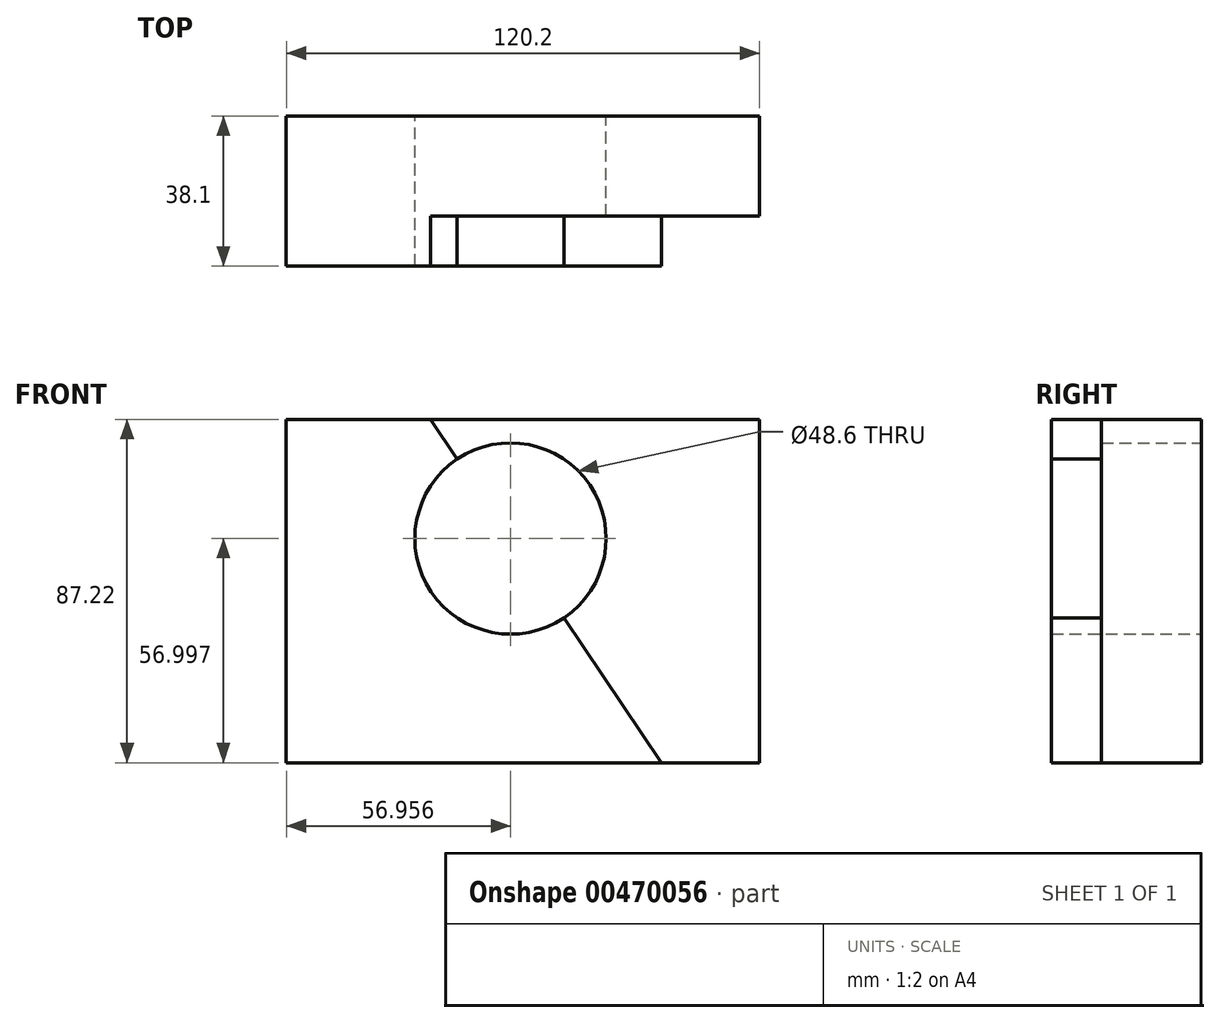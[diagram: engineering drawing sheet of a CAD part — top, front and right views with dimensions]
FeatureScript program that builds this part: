
annotation { "Feature Type Name" : "Feature", "Feature Type Description" : "" }
export const myFeature = defineFeature(function(context is Context, id is Id, definition is map)
    precondition{}
    {
        {
            var Q0;
            Q0=qCreatedBy(makeId("Front.planeOp"),FACE);
            var sketch = newSketch(context, id + "F0", { "sketchPlane" : qUnion([Q0])});
            skLineSegment(sketch, "E0.bottom", {"start": v(60.1, 43.6) * mm, "end": v(-60.1, 43.6) * mm});
            skLineSegment(sketch, "E0.top", {"start": v(60.1, -43.6) * mm, "end": v(-60.1, -43.6) * mm});
            skLineSegment(sketch, "E0.left", {"start": v(60.1, 43.6) * mm, "end": v(60.1, -43.6) * mm});
            skLineSegment(sketch, "E0.right", {"start": v(-60.1, 43.6) * mm, "end": v(-60.1, -43.6) * mm});
            skPoint(sketch, "E0.middle", {"position": v(0, 0) * mm});
            skLineSegment(sketch, "E1", {"start": v(-23.51, 43.6) * mm, "end": v(-16.72, 33.54) * mm});
            skCircle(sketch, "E2", {"center": v(-3.14, 13.39) * mm, "radius": 24.3 * mm});
            skLineSegment(sketch, "E3.trimOffspring", {"start": v(10.44, -6.76) * mm, "end": v(35.27, -43.6) * mm});
            skSolve(sketch);
        }
        {
            var Q0;
            {var subQ0=sQuery(id+"F0.wireOp",EDGE,"E0.right");Q0=makeQuery(id+"F0.imprint","IMPRINT",FACE,{"disambiguationData":[TD([[makeQuery(id+"F0.imprint","IMPRINT",EDGE,{"derivedFrom":subQ0}),1.0]])]});}
            extrude(context, id + "F1", {"entities" : qUnion([Q0]), "depth" : 38.1 * mm});
        }
        {
            var Q0;
            {var subQ1=sQuery(id+"F0.wireOp",EDGE,"E0.left");Q0=makeQuery(id+"F0.imprint","IMPRINT",FACE,{"disambiguationData":[TD([[makeQuery(id+"F0.imprint","IMPRINT",EDGE,{"derivedFrom":subQ1}),-1.0]])]});}
            extrude(context, id + "F2", {"entities" : qUnion([Q0]), "operationType" : NewBodyOperationType.ADD, "depth" : 25.4 * mm});
        }
    });
